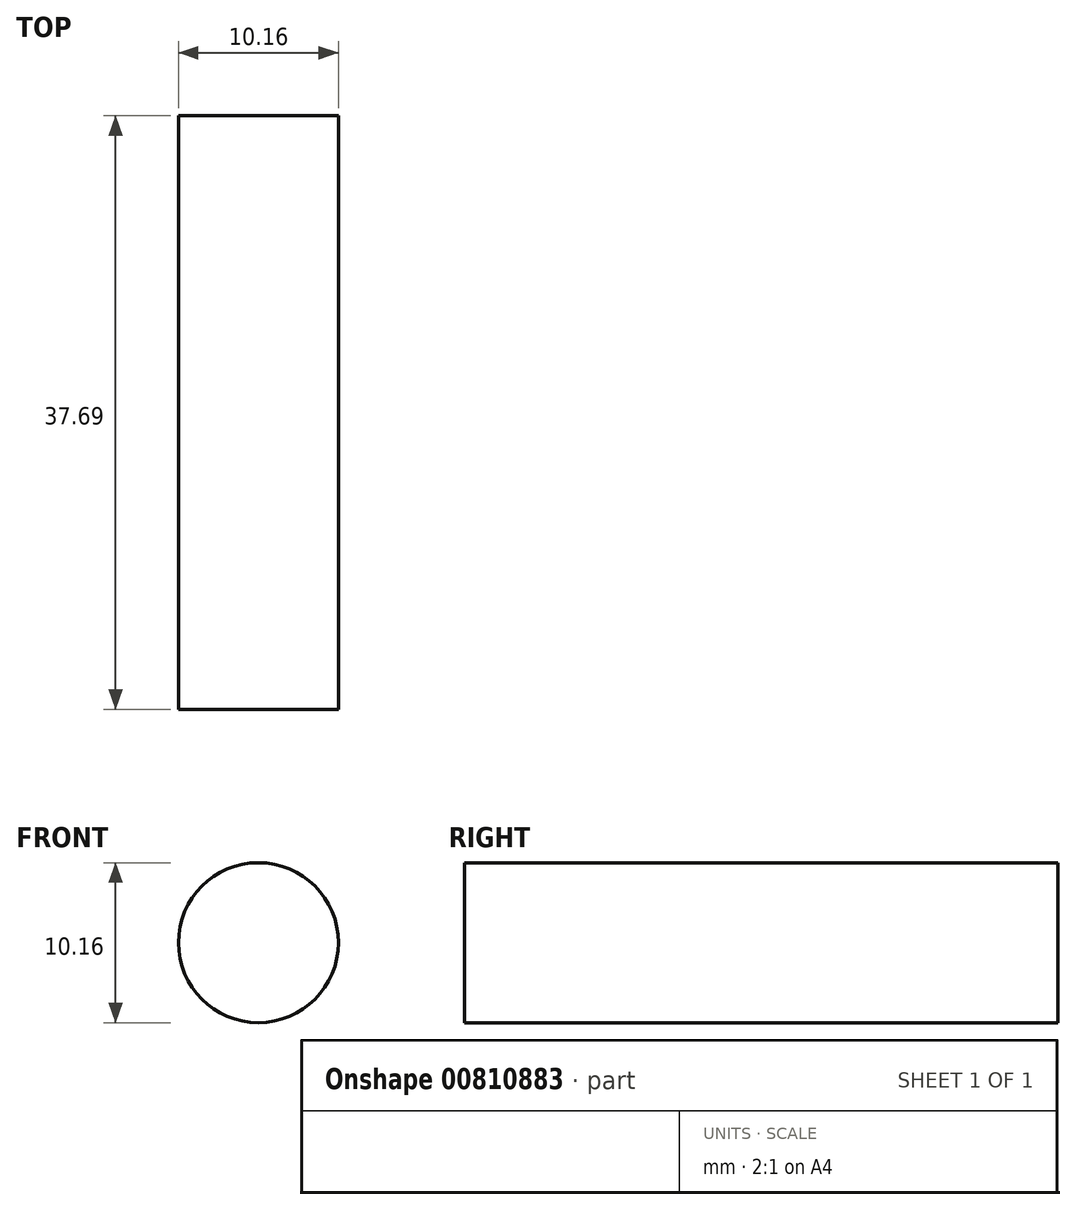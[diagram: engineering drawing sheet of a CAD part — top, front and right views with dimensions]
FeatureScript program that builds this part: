
annotation { "Feature Type Name" : "Feature", "Feature Type Description" : "" }
export const myFeature = defineFeature(function(context is Context, id is Id, definition is map)
    precondition{}
    {
        {
            var Q0;
            Q0=qCreatedBy(makeId("Front.planeOp"),FACE);
            var sketch = newSketch(context, id + "F0", { "sketchPlane" : qUnion([Q0])});
            skCircle(sketch, "E0", {"center": v(0, 0) * mm, "radius": 5.08 * mm});
            skSolve(sketch);
        }
        {
            var Q0;
            Q0 = qSketchRegion(id + "F0", true);
            extrude(context, id + "F1", {"entities" : qUnion([Q0]), "depth" : 37.7 * mm, "offsetDistance" : 25.4 * mm});
        }
    });
